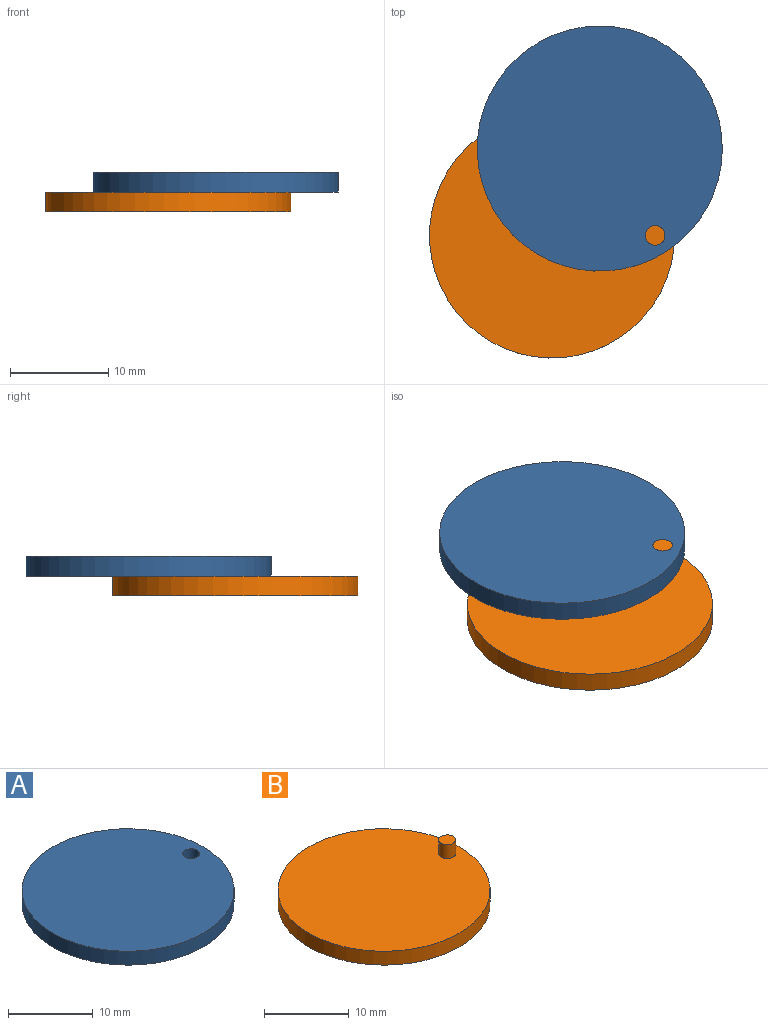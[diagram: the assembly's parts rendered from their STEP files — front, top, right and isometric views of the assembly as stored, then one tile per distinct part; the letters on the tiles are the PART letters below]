
ASSEMBLY  parts=2 mates=1
PART A: 4 faces, bbox 25x25x2 mm
  f0: cylinder r=1mm len=2mm, axis (0,0,-1), area 12.6mm2, adj f2,f3
  f1: cylinder r=12.5mm len=25mm, axis (0,0,-1), area 157.1mm2, adj f2,f3
  f2: plane 25x25mm, normal (0,0,1), area 487.7mm2, adj f0,f1
  f3: plane 25x25mm, normal (0,0,-1), area 487.7mm2, adj f0,f1
PART B: 5 faces, bbox 25x25x4 mm
  f0: cylinder r=12.5mm len=25mm, axis (0,0,-1), area 157.1mm2, adj f1,f2
  f1: plane 25x25mm, normal (0,0,1), area 487.7mm2, adj f0,f3
  f2: plane 25x25mm, normal (0,0,-1), area 490.9mm2, adj f0
  f3: cylinder r=1mm len=2mm, axis (0,0,-1), area 12.6mm2, adj f1,f4
  f4: plane 2x2mm, normal (0,0,1), area 3.1mm2, adj f3
PLACE A rot(axis=(0,0,-1),57.5deg) t=(4.86,8.86,2)mm
PLACE B at identity fixed
MATE revolute B.f3 <-> A.f0  axis (0,0,1) through (10.5,0,4)mm
